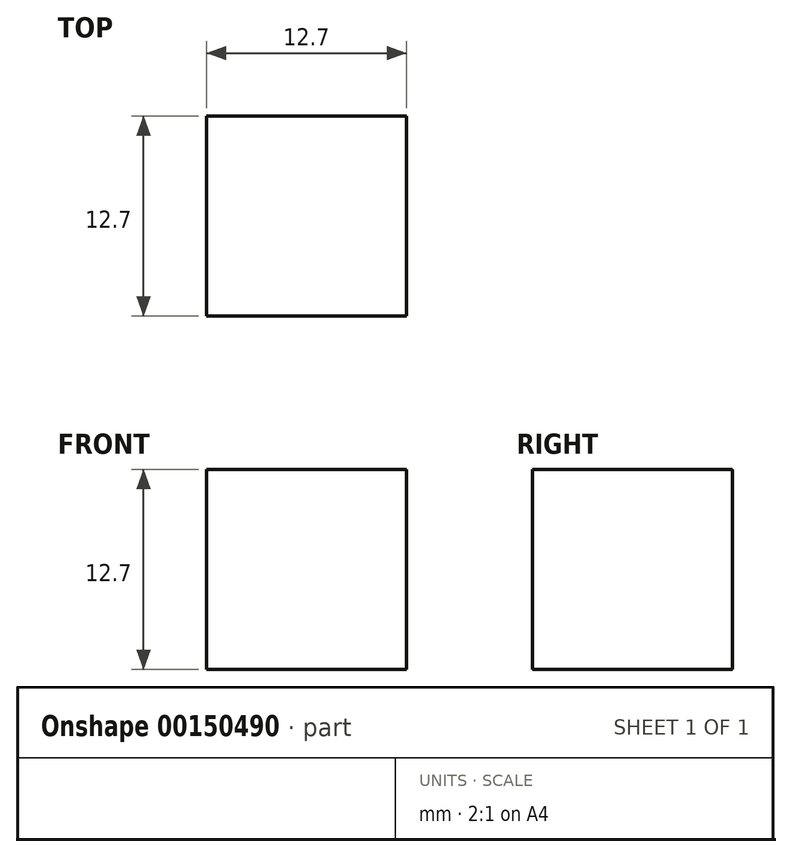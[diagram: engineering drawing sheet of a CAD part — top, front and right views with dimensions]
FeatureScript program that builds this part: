
annotation { "Feature Type Name" : "Feature", "Feature Type Description" : "" }
export const myFeature = defineFeature(function(context is Context, id is Id, definition is map)
    precondition{}
    {
        {
            var Q0;
            Q0=qCreatedBy(makeId("Front.planeOp"),FACE);
            var sketch = newSketch(context, id + "F0", { "sketchPlane" : qUnion([Q0])});
            skLineSegment(sketch, "E0.bottom", {"start": v(6.35, 6.35) * mm, "end": v(-6.35, 6.35) * mm});
            skLineSegment(sketch, "E0.top", {"start": v(6.35, -6.35) * mm, "end": v(-6.35, -6.35) * mm});
            skLineSegment(sketch, "E0.left", {"start": v(6.35, 6.35) * mm, "end": v(6.35, -6.35) * mm});
            skLineSegment(sketch, "E0.right", {"start": v(-6.35, 6.35) * mm, "end": v(-6.35, -6.35) * mm});
            skPoint(sketch, "E0.middle", {"position": v(0, 0) * mm});
            skSolve(sketch);
        }
        {
            var Q0;
            Q0 = qSketchRegion(id + "F0", true);
            extrude(context, id + "F1", {"entities" : qUnion([Q0]), "depth" : 12.7 * mm});
        }
    });
